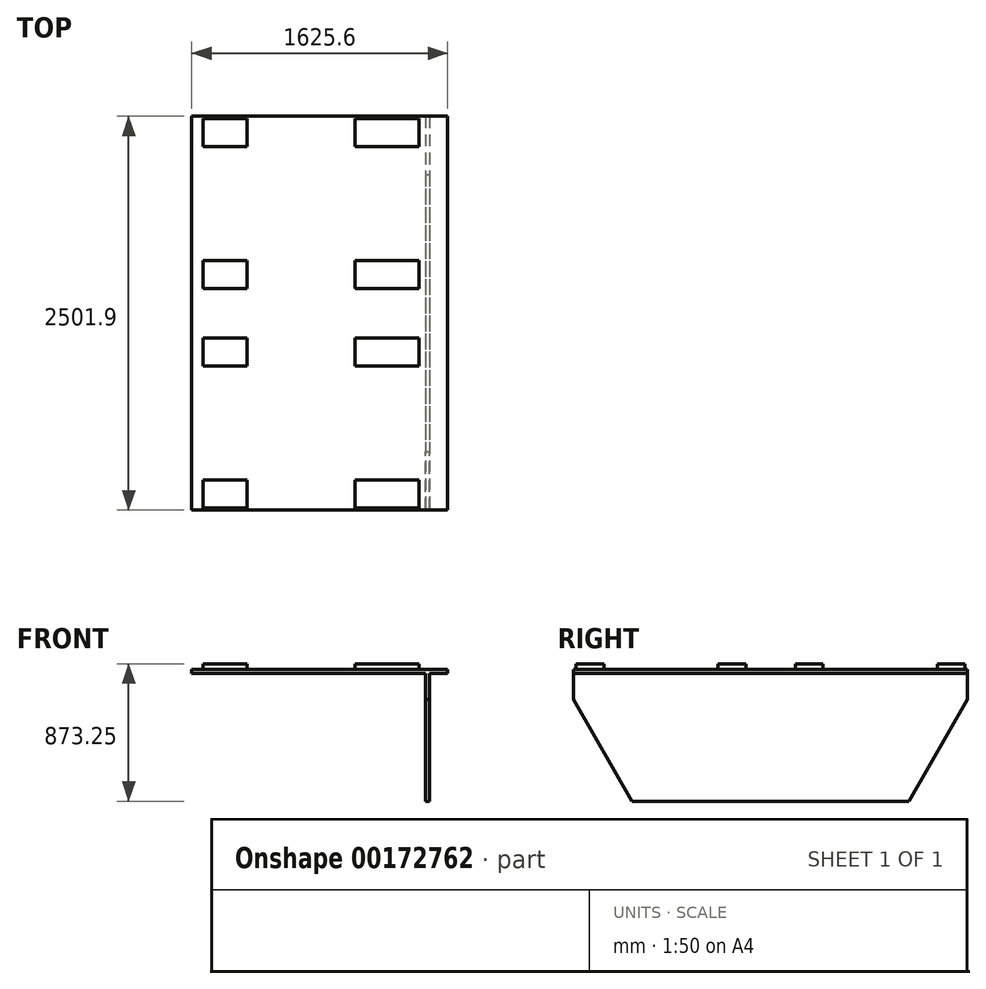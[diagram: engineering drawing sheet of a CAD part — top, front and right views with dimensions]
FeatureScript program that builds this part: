
annotation { "Feature Type Name" : "Feature", "Feature Type Description" : "" }
export const myFeature = defineFeature(function(context is Context, id is Id, definition is map)
    precondition{}
    {
        {
            var Q0;
            Q0=qCreatedBy(makeId("Top.planeOp"),FACE);
            var sketch = newSketch(context, id + "F0", { "sketchPlane" : qUnion([Q0])});
            skLineSegment(sketch, "E0.rect.bottom", {"start": v(-812.8, 1250.95) * mm, "end": v(812.8, 1250.95) * mm});
            skLineSegment(sketch, "E0.rect.top", {"start": v(-812.8, -1250.95) * mm, "end": v(812.8, -1250.95) * mm});
            skLineSegment(sketch, "E0.rect.left", {"start": v(-812.8, 1250.95) * mm, "end": v(-812.8, -1250.95) * mm});
            skLineSegment(sketch, "E0.rect.right", {"start": v(812.8, 1250.95) * mm, "end": v(812.8, -1250.95) * mm});
            skPoint(sketch, "E0.rect.middle", {"position": v(0, 0) * mm});
            skSolve(sketch);
        }
        {
            var Q0;
            Q0=qSketchRegion(id+"F0",true);
            extrude(context, id + "F1", {"entities" : qUnion([Q0]), "depth" : 25.4 * mm});
        }
        {
            var Q0;
            Q0=makeQuery(id+"F1.opExtrude","CAP_FACE",FACE,{"disambiguationData":[OSD([sQuery(id+"F0.wireOp",EDGE,"E0.rect.bottom"),sQuery(id+"F0.wireOp",EDGE,"E0.rect.top"),sQuery(id+"F0.wireOp",EDGE,"E0.rect.left"),sQuery(id+"F0.wireOp",EDGE,"E0.rect.right")])],"isStart":false});
            var sketch = newSketch(context, id + "F2", { "sketchPlane" : qUnion([Q0])});
            skLineSegment(sketch, "E1.0", {"start": v(812.8, 1250.95) * mm, "end": v(812.8, -1250.95) * mm, "construction": true});
            skLineSegment(sketch, "E2.0", {"start": v(-741.43, -1235.2) * mm, "end": v(-462.03, -1235.2) * mm});
            skLineSegment(sketch, "E3.0", {"start": v(-741.43, -1057.4) * mm, "end": v(-462.03, -1057.4) * mm});
            skLineSegment(sketch, "E4.0", {"start": v(-741.43, -333.5) * mm, "end": v(-462.03, -333.5) * mm});
            skLineSegment(sketch, "E5.0", {"start": v(-741.43, -155.7) * mm, "end": v(-462.03, -155.7) * mm});
            skLineSegment(sketch, "E6.1", {"start": v(630.17, -155.7) * mm, "end": v(630.17, -333.5) * mm});
            skLineSegment(sketch, "E7.0", {"start": v(223.77, -155.7) * mm, "end": v(223.77, -333.5) * mm});
            skLineSegment(sketch, "E8.0", {"start": v(-462.03, 0) * mm, "end": v(-462.03, 0) * mm});
            skLineSegment(sketch, "E9.0", {"start": v(-741.43, -155.7) * mm, "end": v(-741.43, -333.5) * mm});
            skLineSegment(sketch, "E10", {"start": v(-812.8, 0) * mm, "end": v(812.8, 0) * mm, "construction": true});
            skPoint(sketch, "E10.endSnap0", {"position": v(-462.03, 0) * mm});
            skPoint(sketch, "E11.orphan", {"position": v(-462.03, 1235.2) * mm});
            skLineSegment(sketch, "E12.trimOffspring", {"start": v(-462.03, -155.7) * mm, "end": v(-462.03, -333.5) * mm});
            skLineSegment(sketch, "E13.trimOffspring", {"start": v(223.77, -333.5) * mm, "end": v(630.17, -333.5) * mm});
            skLineSegment(sketch, "E14.trimOffspring", {"start": v(223.77, -155.7) * mm, "end": v(630.17, -155.7) * mm});
            skLineSegment(sketch, "E15.trimOffspring", {"start": v(-462.03, -1057.4) * mm, "end": v(-462.03, -1235.2) * mm});
            skLineSegment(sketch, "E16.trimOffspring", {"start": v(-741.43, -1057.4) * mm, "end": v(-741.43, -1235.2) * mm});
            skLineSegment(sketch, "E17.trimOffspring", {"start": v(630.17, -1057.4) * mm, "end": v(630.17, -1235.2) * mm});
            skLineSegment(sketch, "E18.trimOffspring", {"start": v(223.77, -1057.4) * mm, "end": v(223.77, -1235.2) * mm});
            skLineSegment(sketch, "E19.trimOffspring", {"start": v(223.77, -1057.4) * mm, "end": v(630.17, -1057.4) * mm});
            skLineSegment(sketch, "E20.trimOffspring", {"start": v(223.77, -1235.2) * mm, "end": v(630.17, -1235.2) * mm});
            skPoint(sketch, "E21.0.start.orphan", {"position": v(-812.8, -1250.95) * mm});
            skLineSegment(sketch, "E22.MirrorCS", {"start": v(223.77, 1057.4) * mm, "end": v(223.77, 1235.2) * mm});
            skLineSegment(sketch, "E23.MirrorCS", {"start": v(630.17, 1057.4) * mm, "end": v(630.17, 1235.2) * mm});
            skLineSegment(sketch, "E24.MirrorCS", {"start": v(-741.43, 1057.4) * mm, "end": v(-741.43, 1235.2) * mm});
            skPoint(sketch, "E25.MirrorP", {"position": v(-812.8, 1250.95) * mm});
            skLineSegment(sketch, "E26.MirrorCS", {"start": v(223.77, 1235.2) * mm, "end": v(630.17, 1235.2) * mm});
            skLineSegment(sketch, "E27.MirrorCS", {"start": v(-741.43, 155.7) * mm, "end": v(-741.43, 333.5) * mm});
            skLineSegment(sketch, "E28.MirrorCS", {"start": v(223.77, 1057.4) * mm, "end": v(630.17, 1057.4) * mm});
            skLineSegment(sketch, "E29.MirrorCS", {"start": v(-462.03, 1057.4) * mm, "end": v(-462.03, 1235.2) * mm});
            skLineSegment(sketch, "E30.MirrorCS", {"start": v(223.77, 155.7) * mm, "end": v(223.77, 333.5) * mm});
            skLineSegment(sketch, "E31.MirrorCS", {"start": v(-741.43, 333.5) * mm, "end": v(-462.03, 333.5) * mm});
            skLineSegment(sketch, "E32.MirrorCS", {"start": v(223.77, 155.7) * mm, "end": v(630.17, 155.7) * mm});
            skLineSegment(sketch, "E33.MirrorCS", {"start": v(630.17, 155.7) * mm, "end": v(630.17, 333.5) * mm});
            skLineSegment(sketch, "E34.MirrorCS", {"start": v(223.77, 333.5) * mm, "end": v(630.17, 333.5) * mm});
            skLineSegment(sketch, "E35.MirrorCS", {"start": v(-741.43, 1057.4) * mm, "end": v(-462.03, 1057.4) * mm});
            skLineSegment(sketch, "E36.MirrorCS", {"start": v(-462.03, 155.7) * mm, "end": v(-462.03, 333.5) * mm});
            skLineSegment(sketch, "E37.MirrorCS", {"start": v(-741.43, 155.7) * mm, "end": v(-462.03, 155.7) * mm});
            skLineSegment(sketch, "E38.MirrorCS", {"start": v(-741.43, 1235.2) * mm, "end": v(-462.03, 1235.2) * mm});
            skSolve(sketch);
        }
        {
            var Q0;
            Q0=qSketchRegion(id+"F2",true);
            extrude(context, id + "F3", {"entities" : qUnion([Q0]), "operationType" : NewBodyOperationType.ADD, "depth" : 35.05 * mm});
        }
        {
            var Q0;
            Q0=makeQuery(id+"F1.opExtrude","SWEPT_FACE",FACE,{"disambiguationData":[OSD([sQuery(id+"F0.wireOp",EDGE,"E0.rect.right")])]});
            cPlane(context, id + "F4", {"entities" : qUnion([Q0]), "cplaneType" : CPlaneType.OFFSET, "offset" : 114.3 * mm, "oppositeDirection" : true, "width" : 152.4 * mm, "height" : 152.4 * mm});
        }
        {
            var Q0;
            Q0=qCreatedBy(id+"F4.planeOp",FACE);
            var sketch = newSketch(context, id + "F5", { "sketchPlane" : qUnion([Q0])});
            skLineSegment(sketch, "E39.0", {"start": v(1250.95, 0) * mm, "end": v(-1250.95, 0) * mm});
            skLineSegment(sketch, "E40.0", {"start": v(1250.95, -812.8) * mm, "end": v(-1250.95, -812.8) * mm});
            skLineSegment(sketch, "E41.0", {"start": v(1250.95, -165.1) * mm, "end": v(-1250.95, -165.1) * mm});
            skLineSegment(sketch, "E42", {"start": v(0, -812.8) * mm, "end": v(0, 431.6) * mm, "construction": true});
            skLineSegment(sketch, "E43.0", {"start": v(-879.47, -812.8) * mm, "end": v(-879.47, 431.6) * mm, "construction": true});
            skLineSegment(sketch, "E44", {"start": v(-1250.95, 0) * mm, "end": v(-1250.95, -165.1) * mm});
            skLineSegment(sketch, "E45", {"start": v(-1250.95, -165.1) * mm, "end": v(-879.47, -812.8) * mm});
            skLineSegment(sketch, "E46.MirrorCS", {"start": v(1250.95, 0) * mm, "end": v(1250.95, -165.1) * mm});
            skLineSegment(sketch, "E47.MirrorCS", {"start": v(1250.95, -165.1) * mm, "end": v(879.48, -812.8) * mm});
            skSolve(sketch);
        }
        {
            var Q0;
            Q0=qSketchRegion(id+"F5",true);
            extrude(context, id + "F6", {"entities" : qUnion([Q0]), "operationType" : NewBodyOperationType.ADD, "oppositeDirection" : true, "depth" : 25.4 * mm});
        }
    });
